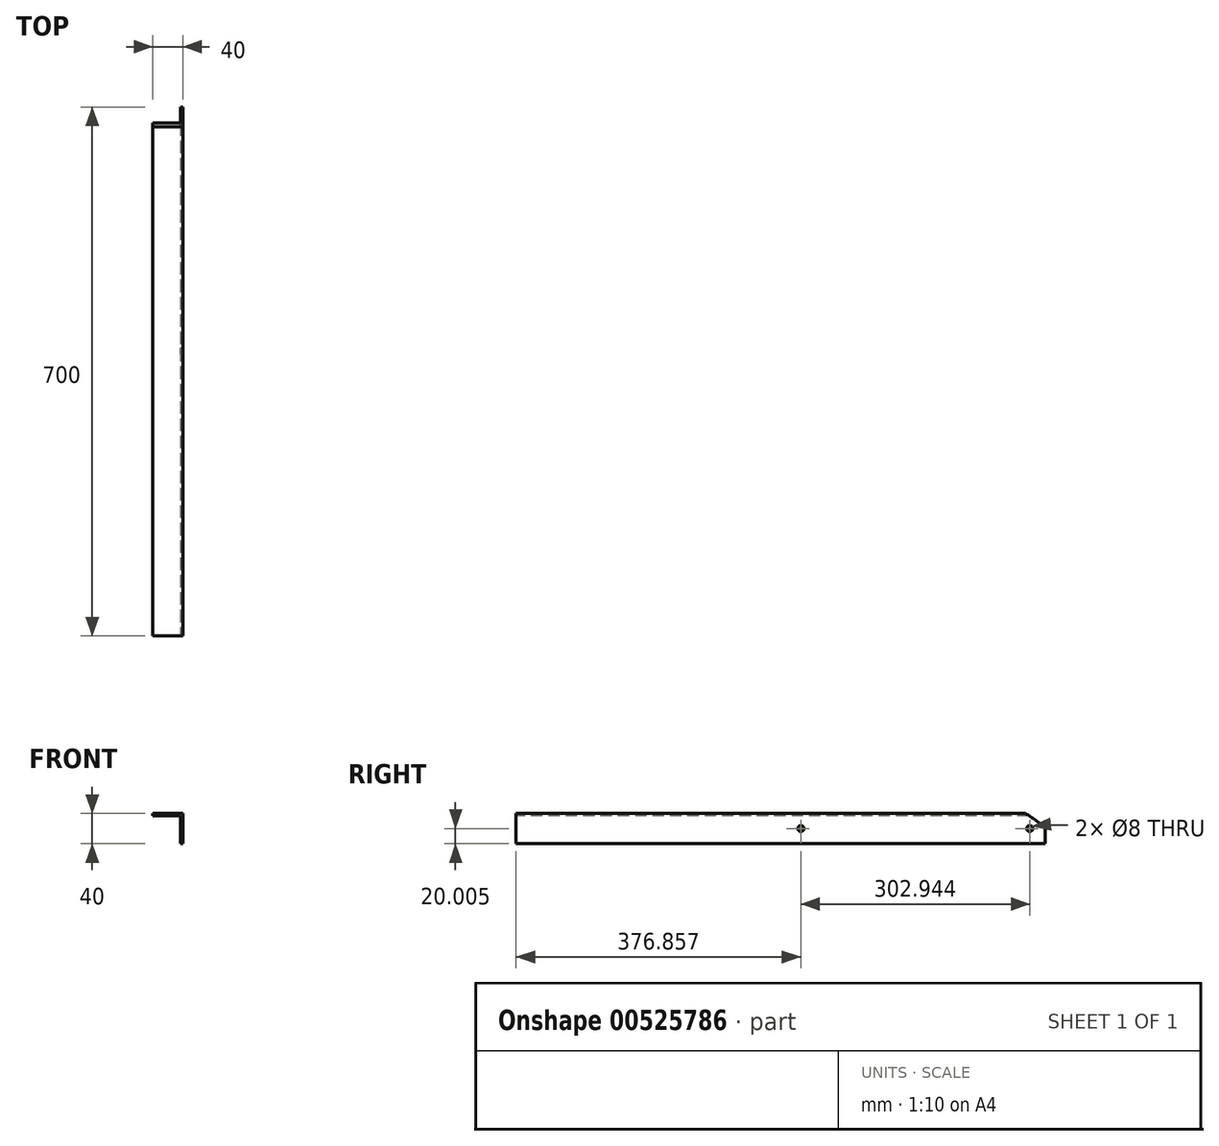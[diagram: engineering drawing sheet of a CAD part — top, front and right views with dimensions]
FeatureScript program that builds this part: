
annotation { "Feature Type Name" : "Feature", "Feature Type Description" : "" }
export const myFeature = defineFeature(function(context is Context, id is Id, definition is map)
    precondition{}
    {
        {
            var Q0;
            Q0=qCreatedBy(makeId("Right.planeOp"),FACE);
            var sketch = newSketch(context, id + "F0", { "sketchPlane" : qUnion([Q0])});
            skArc(sketch, "E0.0", {"start": v(264.63, -46.78) * mm, "mid": v(177.74, 79.37) * mm, "end": v(35.65, 136.58) * mm, "construction": true});
            skCircle(sketch, "E1", {"center": v(-147.81, 73.37) * mm, "radius": 4 * mm});
            skArc(sketch, "E2.trimOffspring", {"start": v(-12.29, 136.58) * mm, "mid": v(-154.38, 79.37) * mm, "end": v(-241.27, -46.78) * mm, "construction": true});
            skCircle(sketch, "E3.MirrorC", {"center": v(155.13, 73.37) * mm, "radius": 4 * mm});
            skLineSegment(sketch, "E4.0", {"start": v(149.3, 93.37) * mm, "end": v(-524.67, 93.37) * mm});
            skLineSegment(sketch, "E5.0", {"start": v(175.33, 53.37) * mm, "end": v(-524.67, 53.37) * mm});
            skArc(sketch, "E6.0", {"start": v(175.33, 74.9) * mm, "mid": v(162.6, 84.53) * mm, "end": v(149.3, 93.37) * mm});
            skLineSegment(sketch, "E7", {"start": v(175.33, 74.9) * mm, "end": v(175.33, 53.37) * mm});
            skLineSegment(sketch, "E8", {"start": v(-524.67, 53.37) * mm, "end": v(-524.67, 93.37) * mm});
            skSolve(sketch);
        }
        {
            var Q0;
            Q0=makeQuery(id+"F0.imprint","IMPRINT",FACE,{"disambiguationData":[TD([[makeQuery(id+"F0.imprint","IMPRINT",EDGE,{"derivedFrom":sQuery(id+"F0.wireOp",EDGE,"E1")}),-1.0]])]});
            extrude(context, id + "F1", {"entities" : qUnion([Q0]), "oppositeDirection" : true, "depth" : 3 * mm, "offsetDistance" : 25 * mm});
        }
        {
            var Q0;
            Q0=makeQuery(id+"F1.opExtrude","CAP_FACE",FACE,{"disambiguationData":[OSD([sQuery(id+"F0.wireOp",EDGE,"E1"),sQuery(id+"F0.wireOp",EDGE,"E3.MirrorC"),sQuery(id+"F0.wireOp",EDGE,"E4.0"),sQuery(id+"F0.wireOp",EDGE,"E5.0"),sQuery(id+"F0.wireOp",EDGE,"E6.0"),sQuery(id+"F0.wireOp",EDGE,"E7"),sQuery(id+"F0.wireOp",EDGE,"E8")])],"isStart":false});
            var sketch = newSketch(context, id + "F2", { "sketchPlane" : qUnion([Q0])});
            skLineSegment(sketch, "E9.0", {"start": v(-154.02, 90.37) * mm, "end": v(524.67, 90.37) * mm});
            skArc(sketch, "E10.0", {"start": v(-175.33, 74.9) * mm, "mid": v(-162.6, 84.53) * mm, "end": v(-149.3, 93.37) * mm});
            skLineSegment(sketch, "E11.0", {"start": v(524.67, 53.37) * mm, "end": v(524.67, 93.37) * mm});
            skLineSegment(sketch, "E12.0", {"start": v(-149.3, 93.37) * mm, "end": v(524.67, 93.37) * mm});
            skSolve(sketch);
        }
        {
            var Q0;
            {var subQ0=sQuery(id+"F2.wireOp",EDGE,"E9.0");Q0=makeQuery(id+"F2.imprint","IMPRINT",FACE,{"disambiguationData":[TD([[makeQuery(id+"F2.imprint","IMPRINT",EDGE,{"derivedFrom":subQ0}),1.0]])]});}
            extrude(context, id + "F3", {"entities" : qUnion([Q0]), "operationType" : NewBodyOperationType.ADD, "depth" : 37 * mm, "offsetDistance" : 25 * mm});
        }
    });
